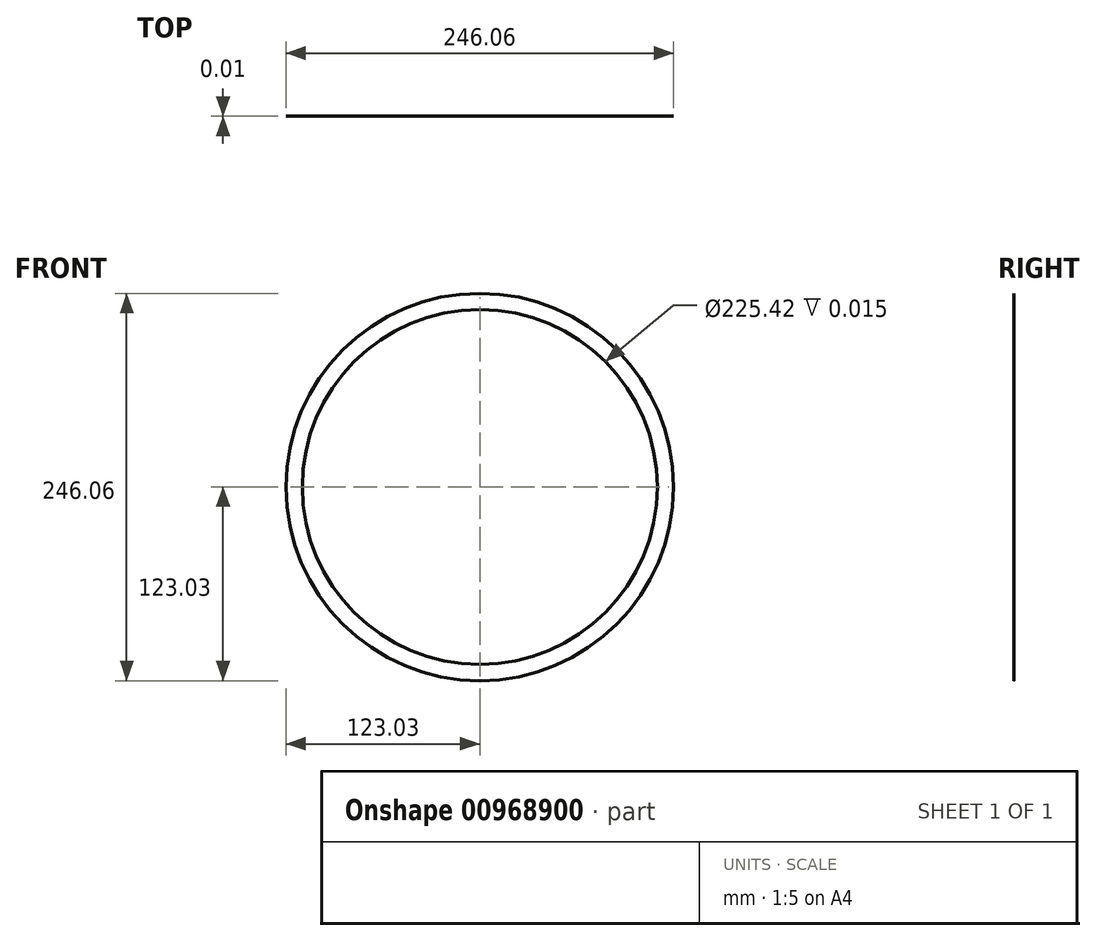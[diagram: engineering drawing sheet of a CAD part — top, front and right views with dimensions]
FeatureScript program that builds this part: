
annotation { "Feature Type Name" : "Feature", "Feature Type Description" : "" }
export const myFeature = defineFeature(function(context is Context, id is Id, definition is map)
    precondition{}
    {
        {
            var Q0;
            Q0=qCreatedBy(makeId("Front.planeOp"),FACE);
            var sketch = newSketch(context, id + "F0", { "sketchPlane" : qUnion([Q0])});
            skCircle(sketch, "E0", {"center": v(0, 0) * mm, "radius": 123.03 * mm});
            skCircle(sketch, "E1", {"center": v(0, 0) * mm, "radius": 112.71 * mm});
            skSolve(sketch);
        }
        {
            var Q0;
            Q0=makeQuery(id+"F0.imprint","IMPRINT",FACE,{"disambiguationData":[TD([[makeQuery(id+"F0.imprint","IMPRINT",EDGE,{"derivedFrom":sQuery(id+"F0.wireOp",EDGE,"E0")}),1.0]])]});
            extrude(context, id + "F1", {"entities" : qUnion([Q0]), "depth" : 3 / 203.2 * mm, "offsetDistance" : 25.4 * mm});
        }
    });
